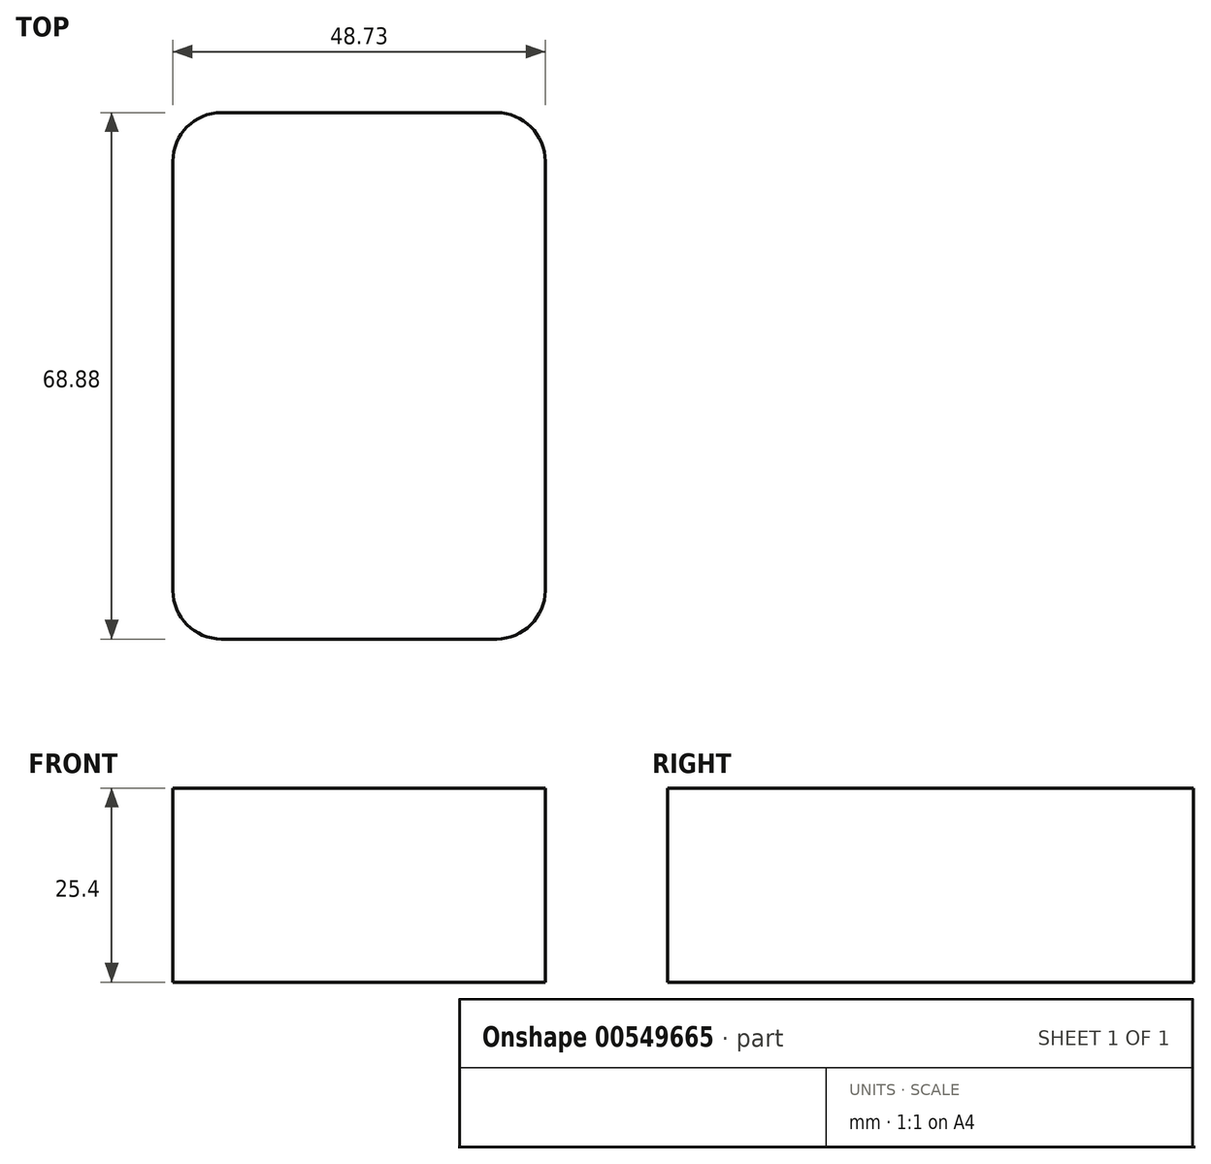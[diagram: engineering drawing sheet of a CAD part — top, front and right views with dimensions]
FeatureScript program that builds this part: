
annotation { "Feature Type Name" : "Feature", "Feature Type Description" : "" }
export const myFeature = defineFeature(function(context is Context, id is Id, definition is map)
    precondition{}
    {
        {
            var Q0;
            Q0=qCreatedBy(makeId("Top.planeOp"),FACE);
            var sketch = newSketch(context, id + "F0", { "sketchPlane" : qUnion([Q0])});
            skLineSegment(sketch, "E0.bottom", {"start": v(6.35, 0) * mm, "end": v(42.38, 0) * mm});
            skLineSegment(sketch, "E0.top", {"start": v(6.35, 68.88) * mm, "end": v(42.38, 68.88) * mm});
            skLineSegment(sketch, "E0.left", {"start": v(0, 6.35) * mm, "end": v(0, 62.53) * mm});
            skLineSegment(sketch, "E0.right", {"start": v(48.73, 6.35) * mm, "end": v(48.73, 62.53) * mm});
            skPoint(sketch, "E1.visualSharp", {"position": v(0, 68.88) * mm});
            skArc(sketch, "E1.filletArc", {"start": v(6.35, 68.88) * mm, "mid": v(1.86, 67.02) * mm, "end": v(0, 62.53) * mm});
            skPoint(sketch, "E2.visualSharp", {"position": v(48.73, 0) * mm});
            skArc(sketch, "E2.filletArc", {"start": v(42.38, 0) * mm, "mid": v(46.87, 1.86) * mm, "end": v(48.73, 6.35) * mm});
            skPoint(sketch, "E3.visualSharp", {"position": v(0, 0) * mm});
            skArc(sketch, "E3.filletArc", {"start": v(0, 6.35) * mm, "mid": v(1.86, 1.86) * mm, "end": v(6.35, 0) * mm});
            skPoint(sketch, "E4.visualSharp", {"position": v(48.73, 68.88) * mm});
            skArc(sketch, "E4.filletArc", {"start": v(48.73, 62.53) * mm, "mid": v(46.87, 67.02) * mm, "end": v(42.38, 68.88) * mm});
            skSolve(sketch);
        }
        {
            var Q0;
            Q0 = qSketchRegion(id + "F0", true);
            extrude(context, id + "F1", {"entities" : qUnion([Q0]), "depth" : 25.4 * mm, "offsetDistance" : 25.4 * mm});
        }
        {
            var Q0;
            Q0=makeQuery(id+"F1.opExtrude","CAP_EDGE",EDGE,{"disambiguationData":[OSD([sQuery(id+"F0.wireOp",EDGE,"E1.filletArc")])],"isStart":false});
            var Q1;
            Q1=makeQuery(id+"F1.opExtrude","CAP_VERTEX",VERTEX,{"disambiguationData":[OSD([sQuery(id+"F0.wireOp",EDGE,"E0.left"),sQuery(id+"F0.wireOp",EDGE,"E1.filletArc")])],"isStart":false});
            cPlane(context, id + "F2", {"entities" : qUnion([Q0, Q1]), "cplaneType" : CPlaneType.CURVE_POINT, "offset" : 25.4 * mm, "width" : 152.4 * mm, "height" : 152.4 * mm});
        }
    });
